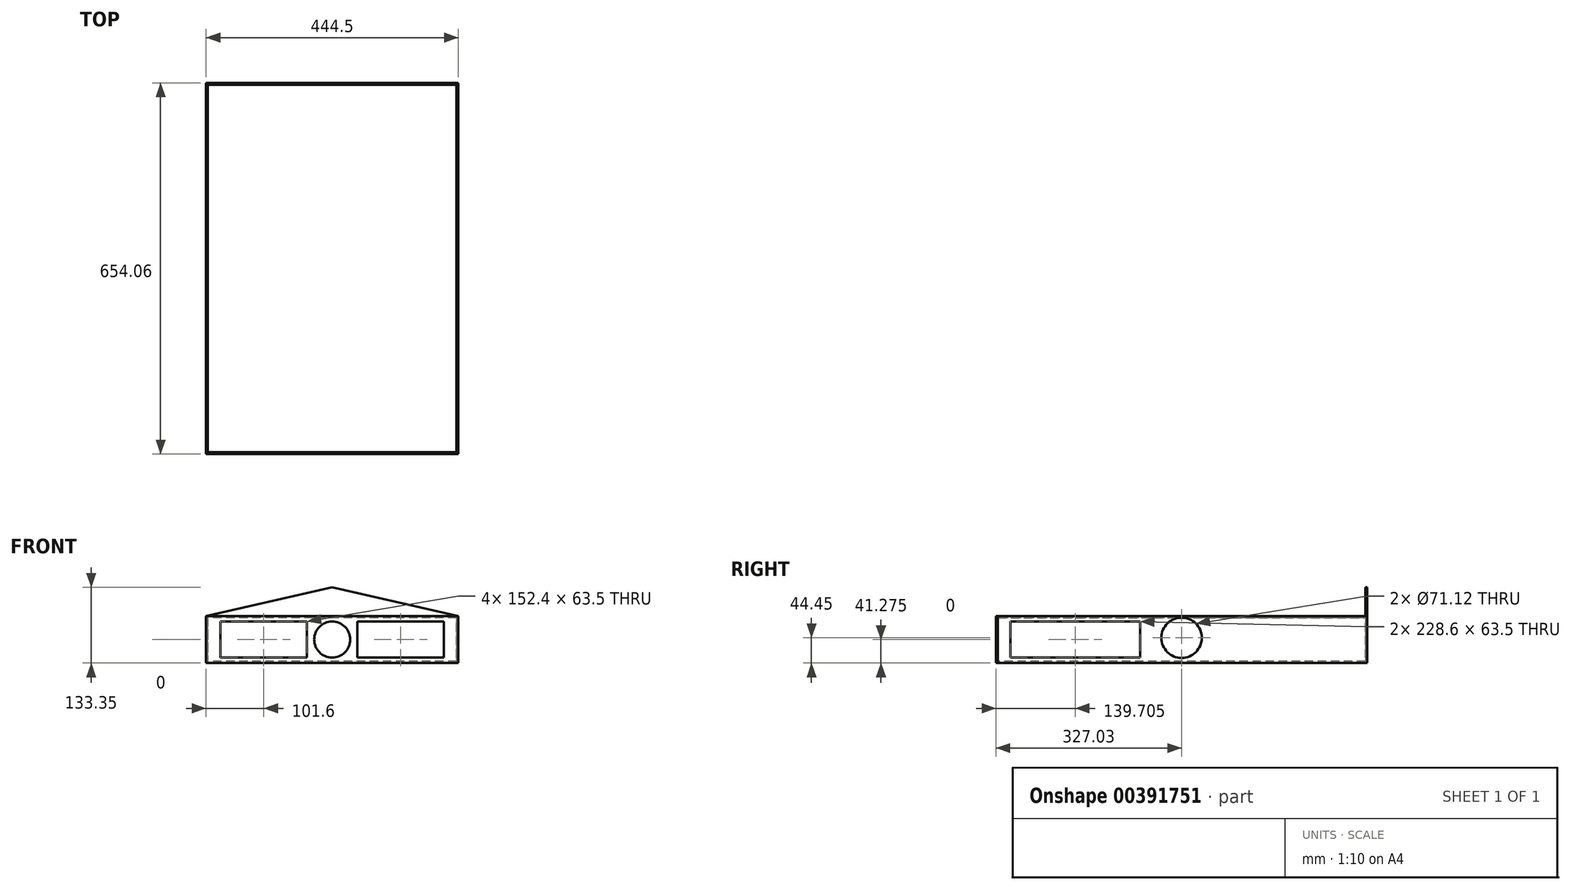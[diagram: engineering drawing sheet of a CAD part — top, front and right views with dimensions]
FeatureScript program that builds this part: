
annotation { "Feature Type Name" : "Feature", "Feature Type Description" : "" }
export const myFeature = defineFeature(function(context is Context, id is Id, definition is map)
    precondition{}
    {
        {
            var Q0;
            Q0=qCreatedBy(makeId("Top.planeOp"),FACE);
            var sketch = newSketch(context, id + "F0", { "sketchPlane" : qUnion([Q0])});
            skLineSegment(sketch, "E0.bottom", {"start": v(219.08, 323.85) * mm, "end": v(-219.07, 323.85) * mm});
            skLineSegment(sketch, "E0.top", {"start": v(219.07, -323.85) * mm, "end": v(-219.08, -323.85) * mm});
            skLineSegment(sketch, "E0.left", {"start": v(219.08, 323.85) * mm, "end": v(219.07, -323.85) * mm});
            skLineSegment(sketch, "E0.right", {"start": v(-219.07, 323.85) * mm, "end": v(-219.08, -323.85) * mm});
            skPoint(sketch, "E0.middle", {"position": v(0, 0) * mm});
            skSolve(sketch);
        }
        {
            var Q0;
            Q0=qSketchRegion(id+"F0",true);
            extrude(context, id + "F1", {"entities" : qUnion([Q0]), "depth" : 3.17 * mm});
        }
        {
            var Q0;
            Q0=makeQuery(id+"F1.opExtrude","CAP_FACE",FACE,{"disambiguationData":[OSD([sQuery(id+"F0.wireOp",EDGE,"E0.bottom"),sQuery(id+"F0.wireOp",EDGE,"E0.top"),sQuery(id+"F0.wireOp",EDGE,"E0.left"),sQuery(id+"F0.wireOp",EDGE,"E0.right")])],"isStart":true});
            var sketch = newSketch(context, id + "F2", { "sketchPlane" : qUnion([Q0])});
            skLineSegment(sketch, "E1.bottom", {"start": v(222.25, 327.03) * mm, "end": v(-222.25, 327.03) * mm});
            skLineSegment(sketch, "E1.top", {"start": v(222.25, -327.03) * mm, "end": v(-222.25, -327.03) * mm});
            skLineSegment(sketch, "E1.left", {"start": v(222.25, 327.03) * mm, "end": v(222.25, -327.03) * mm});
            skLineSegment(sketch, "E1.right", {"start": v(-222.25, 327.03) * mm, "end": v(-222.25, -327.03) * mm});
            skPoint(sketch, "E1.middle", {"position": v(0, 0) * mm});
            skLineSegment(sketch, "E2.bottom", {"start": v(219.07, 323.85) * mm, "end": v(-219.07, 323.85) * mm});
            skLineSegment(sketch, "E2.top", {"start": v(219.07, -323.85) * mm, "end": v(-219.07, -323.85) * mm});
            skLineSegment(sketch, "E2.left", {"start": v(219.07, 323.85) * mm, "end": v(219.07, -323.85) * mm});
            skLineSegment(sketch, "E2.right", {"start": v(-219.07, 323.85) * mm, "end": v(-219.07, -323.85) * mm});
            skLineSegment(sketch, "E3", {"start": v(219.07, 323.85) * mm, "end": v(222.25, 323.85) * mm});
            skLineSegment(sketch, "E4", {"start": v(-219.07, 323.85) * mm, "end": v(-222.25, 323.85) * mm});
            skLineSegment(sketch, "E5", {"start": v(-219.07, -323.85) * mm, "end": v(-222.25, -323.85) * mm});
            skLineSegment(sketch, "E6", {"start": v(219.07, -323.85) * mm, "end": v(222.25, -321.74) * mm});
            skSolve(sketch);
        }
        {
            var Q0;
            {var subQ1=sQuery(id+"F2.wireOp",EDGE,"E1.bottom");Q0=makeQuery(id+"F2.imprint","IMPRINT",FACE,{"disambiguationData":[TD([[makeQuery(id+"F2.imprint","IMPRINT",EDGE,{"derivedFrom":subQ1}),1.0]])]});}
            var Q1;
            {var subQ1=sQuery(id+"F2.wireOp",EDGE,"E1.top");Q1=makeQuery(id+"F2.imprint","IMPRINT",FACE,{"disambiguationData":[TD([[makeQuery(id+"F2.imprint","IMPRINT",EDGE,{"derivedFrom":subQ1}),-1.0]])]});}
            var Q2;
            Q2=makeQuery(id+"F1.opExtrude","CAP_FACE",FACE,{"disambiguationData":[OSD([sQuery(id+"F0.wireOp",EDGE,"E0.bottom"),sQuery(id+"F0.wireOp",EDGE,"E0.top"),sQuery(id+"F0.wireOp",EDGE,"E0.left"),sQuery(id+"F0.wireOp",EDGE,"E0.right")])],"isStart":false});
            extrude(context, id + "F3", {"entities" : qUnion([Q0, Q1]), "oppositeDirection" : true, "depth" : 82.55 * mm});
        }
        {
            var Q0;
            Q0=makeQuery(id+"F2.imprint","IMPRINT",FACE,{"disambiguationData":[TD([[makeQuery(id+"F2.imprint","IMPRINT",EDGE,{"derivedFrom":sQuery(id+"F2.wireOp",EDGE,"E2.left")}),-1.0]])]});
            var Q1;
            Q1=makeQuery(id+"F2.imprint","IMPRINT",FACE,{"disambiguationData":[TD([[makeQuery(id+"F2.imprint","IMPRINT",EDGE,{"derivedFrom":sQuery(id+"F2.wireOp",EDGE,"E2.right")}),1.0]])]});
            var Q2;
            Q2=makeQuery(id+"F3.opExtrude","CAP_FACE",FACE,{"disambiguationData":[OSD([sQuery(id+"F2.wireOp",EDGE,"E1.top"),sQuery(id+"F2.wireOp",EDGE,"E1.left"),sQuery(id+"F2.wireOp",EDGE,"E1.right"),sQuery(id+"F2.wireOp",EDGE,"E2.top"),sQuery(id+"F2.wireOp",EDGE,"E5"),sQuery(id+"F2.wireOp",EDGE,"E6")])],"isStart":false});
            extrude(context, id + "F4", {"entities" : qUnion([Q0, Q1]), "endBound" : BoundingType.UP_TO_SURFACE, "oppositeDirection" : true, "endBoundEntityFace" : qUnion([Q2]), "depth" : 25.4 * mm});
        }
        {
            var Q0;
            Q0=makeQuery(id+"F4.opExtrude","SWEPT_FACE",FACE,{"disambiguationData":[OSD([sQuery(id+"F2.wireOp",EDGE,"E1.right")])]});
            var sketch = newSketch(context, id + "F5", { "sketchPlane" : qUnion([Q0])});
            skCircle(sketch, "E7", {"center": v(0, 44.45) * mm, "radius": 35.56 * mm});
            skSolve(sketch);
        }
        {
            var Q0;
            Q0=makeQuery(id+"F5.imprint","IMPRINT",FACE,{"disambiguationData":[TD([[makeQuery(id+"F5.imprint","IMPRINT",EDGE,{"derivedFrom":sQuery(id+"F5.wireOp",EDGE,"E7")}),1.0]])]});
            extrude(context, id + "F6", {"entities" : qUnion([Q0]), "operationType" : NewBodyOperationType.REMOVE, "endBound" : BoundingType.THROUGH_ALL, "oppositeDirection" : true, "depth" : 25.4 * mm});
        }
        {
            var Q0;
            Q0=makeQuery(id+"F4.opExtrude","SWEPT_FACE",FACE,{"disambiguationData":[OSD([sQuery(id+"F2.wireOp",EDGE,"E1.right")])]});
            var sketch = newSketch(context, id + "F7", { "sketchPlane" : qUnion([Q0])});
            skLineSegment(sketch, "E8.bottom", {"start": v(200.03, 73.03) * mm, "end": v(301.63, 73.03) * mm});
            skLineSegment(sketch, "E8.top", {"start": v(200.03, 47.63) * mm, "end": v(301.63, 47.63) * mm});
            skLineSegment(sketch, "E8.left", {"start": v(200.03, 73.03) * mm, "end": v(200.03, 47.63) * mm});
            skLineSegment(sketch, "E8.right", {"start": v(301.63, 73.03) * mm, "end": v(301.63, 47.63) * mm});
            skLineSegment(sketch, "E9.bottom", {"start": v(263.53, 34.92) * mm, "end": v(301.63, 34.92) * mm});
            skLineSegment(sketch, "E9.top", {"start": v(263.53, 9.53) * mm, "end": v(301.63, 9.53) * mm});
            skLineSegment(sketch, "E9.left", {"start": v(263.53, 34.92) * mm, "end": v(263.53, 9.52) * mm});
            skLineSegment(sketch, "E9.right", {"start": v(301.63, 34.92) * mm, "end": v(301.63, 9.52) * mm});
            skLineSegment(sketch, "E10", {"start": v(250.83, 47.63) * mm, "end": v(250.83, 34.92) * mm, "construction": true});
            skLineSegment(sketch, "E11", {"start": v(250.83, 34.92) * mm, "end": v(263.53, 34.92) * mm, "construction": true});
            skLineSegment(sketch, "E12.bottom", {"start": v(238.13, 34.92) * mm, "end": v(136.53, 34.92) * mm});
            skLineSegment(sketch, "E12.top", {"start": v(238.13, 9.53) * mm, "end": v(136.53, 9.52) * mm});
            skLineSegment(sketch, "E12.left", {"start": v(238.13, 34.92) * mm, "end": v(238.13, 9.53) * mm});
            skLineSegment(sketch, "E12.right", {"start": v(136.53, 34.92) * mm, "end": v(136.53, 9.52) * mm});
            skLineSegment(sketch, "E13", {"start": v(238.13, 34.92) * mm, "end": v(250.83, 34.92) * mm, "construction": true});
            skLineSegment(sketch, "E14", {"start": v(263.53, 9.53) * mm, "end": v(263.53, 0) * mm, "construction": true});
            skLineSegment(sketch, "E15", {"start": v(250.83, 73.03) * mm, "end": v(250.83, 82.55) * mm, "construction": true});
            skLineSegment(sketch, "E16.bottom", {"start": v(174.63, 73.03) * mm, "end": v(73.03, 73.03) * mm});
            skLineSegment(sketch, "E16.top", {"start": v(174.63, 47.63) * mm, "end": v(73.03, 47.63) * mm});
            skLineSegment(sketch, "E16.left", {"start": v(174.63, 73.03) * mm, "end": v(174.63, 47.63) * mm});
            skLineSegment(sketch, "E16.right", {"start": v(73.03, 73.03) * mm, "end": v(73.03, 47.63) * mm});
            skLineSegment(sketch, "E17", {"start": v(174.63, 60.33) * mm, "end": v(187.33, 60.33) * mm, "construction": true});
            skLineSegment(sketch, "E18", {"start": v(187.33, 60.33) * mm, "end": v(200.03, 60.33) * mm, "construction": true});
            skLineSegment(sketch, "E19.bottom", {"start": v(73.03, 34.92) * mm, "end": v(111.13, 34.92) * mm});
            skLineSegment(sketch, "E19.top", {"start": v(73.03, 9.52) * mm, "end": v(111.13, 9.52) * mm});
            skLineSegment(sketch, "E19.left", {"start": v(73.03, 34.92) * mm, "end": v(73.03, 9.52) * mm});
            skLineSegment(sketch, "E19.right", {"start": v(111.13, 34.92) * mm, "end": v(111.13, 9.52) * mm});
            skLineSegment(sketch, "E20", {"start": v(174.63, 73.03) * mm, "end": v(200.03, 73.03) * mm});
            skLineSegment(sketch, "E21", {"start": v(111.13, 9.52) * mm, "end": v(136.53, 9.52) * mm});
            skLineSegment(sketch, "E22", {"start": v(73.03, 34.92) * mm, "end": v(73.03, 47.63) * mm});
            skLineSegment(sketch, "E23", {"start": v(301.63, 47.63) * mm, "end": v(301.63, 34.92) * mm});
            skLineSegment(sketch, "E24", {"start": v(238.13, 9.53) * mm, "end": v(263.53, 9.53) * mm});
            skSolve(sketch);
        }
        {
            var Q0;
            Q0=qSketchRegion(id+"F7",true);
            extrude(context, id + "F8", {"entities" : qUnion([Q0]), "operationType" : NewBodyOperationType.REMOVE, "endBound" : BoundingType.THROUGH_ALL, "oppositeDirection" : true, "depth" : 25.4 * mm});
        }
        {
            var Q0;
            Q0=makeQuery(id+"F3.opExtrude","SWEPT_FACE",FACE,{"disambiguationData":[OSD([sQuery(id+"F2.wireOp",EDGE,"E1.bottom")])]});
            var sketch = newSketch(context, id + "F9", { "sketchPlane" : qUnion([Q0])});
            skLineSegment(sketch, "E25.bottom", {"start": v(-196.85, 73.03) * mm, "end": v(196.85, 73.03) * mm});
            skLineSegment(sketch, "E25.top", {"start": v(-196.85, 9.52) * mm, "end": v(196.85, 9.52) * mm});
            skLineSegment(sketch, "E25.left", {"start": v(-196.85, 73.03) * mm, "end": v(-196.85, 9.52) * mm});
            skLineSegment(sketch, "E25.right", {"start": v(196.85, 73.03) * mm, "end": v(196.85, 9.52) * mm});
            skPoint(sketch, "E25.middle", {"position": v(0, 41.28) * mm});
            skLineSegment(sketch, "E26.bottom", {"start": v(6.35, 73.03) * mm, "end": v(-6.35, 73.03) * mm});
            skLineSegment(sketch, "E26.top", {"start": v(6.35, 9.52) * mm, "end": v(-6.35, 9.52) * mm});
            skLineSegment(sketch, "E26.left", {"start": v(6.35, 73.03) * mm, "end": v(6.35, 9.52) * mm});
            skLineSegment(sketch, "E26.right", {"start": v(-6.35, 73.03) * mm, "end": v(-6.35, 9.52) * mm});
            skCircle(sketch, "E27", {"center": v(0, 41.28) * mm, "radius": 31.75 * mm});
            skLineSegment(sketch, "E28.bottom", {"start": v(44.45, 73.03) * mm, "end": v(-44.45, 73.03) * mm});
            skLineSegment(sketch, "E28.top", {"start": v(44.45, 9.52) * mm, "end": v(-44.45, 9.52) * mm});
            skLineSegment(sketch, "E28.left", {"start": v(44.45, 73.03) * mm, "end": v(44.45, 9.52) * mm});
            skLineSegment(sketch, "E28.right", {"start": v(-44.45, 73.03) * mm, "end": v(-44.45, 9.52) * mm});
            skSolve(sketch);
        }
        {
            var Q0;
            {var subQ0=sQuery(id+"F9.wireOp",EDGE,"E25.left");Q0=makeQuery(id+"F9.imprint","IMPRINT",FACE,{"disambiguationData":[TD([[makeQuery(id+"F9.imprint","IMPRINT",EDGE,{"derivedFrom":subQ0}),1.0]])]});}
            var Q1;
            {var subQ0=sQuery(id+"F9.wireOp",EDGE,"E25.right");Q1=makeQuery(id+"F9.imprint","IMPRINT",FACE,{"disambiguationData":[TD([[makeQuery(id+"F9.imprint","IMPRINT",EDGE,{"derivedFrom":subQ0}),-1.0]])]});}
            var Q2;
            {var subQ0=sQuery(id+"F9.wireOp",EDGE,"E27");var subQ1=sQuery(id+"F9.wireOp",EDGE,"E26.right");var subQ2=makeQuery(id+"F9.imprint","INTERSECT",VERTEX,{"disambiguationData":[OD(0.0)],"derivedFrom":[subQ1,subQ0]});Q2=makeQuery(id+"F9.imprint","IMPRINT",FACE,{"disambiguationData":[TD([[makeQuery(id+"F9.imprint","IMPRINT",EDGE,{"disambiguationData":[TD([[subQ2,-1.0]])],"derivedFrom":subQ1}),-1.0]])]});}
            var Q3;
            {var subQ0=sQuery(id+"F9.wireOp",EDGE,"E27");var subQ5=sQuery(id+"F9.wireOp",EDGE,"E26.left");var subQ6=makeQuery(id+"F9.imprint","INTERSECT",VERTEX,{"disambiguationData":[OD(0.0)],"derivedFrom":[subQ5,subQ0]});Q3=makeQuery(id+"F9.imprint","IMPRINT",FACE,{"disambiguationData":[TD([[makeQuery(id+"F9.imprint","IMPRINT",EDGE,{"disambiguationData":[TD([[subQ6,-1.0]])],"derivedFrom":subQ5}),-1.0]])]});}
            var Q4;
            {var subQ0=sQuery(id+"F9.wireOp",EDGE,"E27");var subQ1=sQuery(id+"F9.wireOp",EDGE,"E26.left");var subQ2=makeQuery(id+"F9.imprint","INTERSECT",VERTEX,{"disambiguationData":[OD(0.0)],"derivedFrom":[subQ1,subQ0]});Q4=makeQuery(id+"F9.imprint","IMPRINT",FACE,{"disambiguationData":[TD([[makeQuery(id+"F9.imprint","IMPRINT",EDGE,{"disambiguationData":[TD([[subQ2,-1.0]])],"derivedFrom":subQ1}),1.0]])]});}
            extrude(context, id + "F10", {"entities" : qUnion([Q0, Q1, Q2, Q3, Q4]), "operationType" : NewBodyOperationType.REMOVE, "endBound" : BoundingType.THROUGH_ALL, "oppositeDirection" : true, "depth" : 25.4 * mm});
        }
        {
            var Q0;
            Q0=makeQuery(id+"F4.opExtrude","CAP_FACE",FACE,{"disambiguationData":[OSD([sQuery(id+"F2.wireOp",EDGE,"E1.left"),sQuery(id+"F2.wireOp",EDGE,"E2.left"),sQuery(id+"F2.wireOp",EDGE,"E3"),sQuery(id+"F2.wireOp",EDGE,"E6")])],"isStart":true});
            var sketch = newSketch(context, id + "F11", { "sketchPlane" : qUnion([Q0])});
            skLineSegment(sketch, "E29.bottom", {"start": v(219.07, 323.85) * mm, "end": v(-219.08, 323.85) * mm});
            skLineSegment(sketch, "E29.top", {"start": v(219.08, -323.85) * mm, "end": v(-219.07, -323.85) * mm});
            skLineSegment(sketch, "E29.left", {"start": v(219.07, 323.85) * mm, "end": v(219.08, -323.85) * mm});
            skLineSegment(sketch, "E29.right", {"start": v(-219.08, 323.85) * mm, "end": v(-219.07, -323.85) * mm});
            skSolve(sketch);
        }
        {
            var Q0;
            Q0=qSketchRegion(id+"F11",true);
            extrude(context, id + "F12", {"entities" : qUnion([Q0]), "oppositeDirection" : true, "depth" : 79.38 * mm});
        }
        {
            var Q0;
            Q0=makeQuery(id+"F3.opExtrude","SWEPT_FACE",FACE,{"disambiguationData":[OSD([sQuery(id+"F2.wireOp",EDGE,"E1.top")])]});
            var sketch = newSketch(context, id + "F13", { "sketchPlane" : qUnion([Q0])});
            skLineSegment(sketch, "E30", {"start": v(-222.25, 82.55) * mm, "end": v(0, 133.35) * mm});
            skLineSegment(sketch, "E31", {"start": v(0, 133.35) * mm, "end": v(222.25, 82.55) * mm});
            skLineSegment(sketch, "E32", {"start": v(222.25, 82.55) * mm, "end": v(-222.25, 82.55) * mm});
            skLineSegment(sketch, "E33", {"start": v(0, 133.35) * mm, "end": v(0, 82.55) * mm});
            skSolve(sketch);
        }
        {
            var Q0;
            {var subQ0=sQuery(id+"F13.wireOp",EDGE,"E31");Q0=makeQuery(id+"F13.imprint","IMPRINT",FACE,{"disambiguationData":[TD([[makeQuery(id+"F13.imprint","IMPRINT",EDGE,{"derivedFrom":subQ0}),-1.0]])]});}
            var Q1;
            {var subQ0=sQuery(id+"F13.wireOp",EDGE,"E30");Q1=makeQuery(id+"F13.imprint","IMPRINT",FACE,{"disambiguationData":[TD([[makeQuery(id+"F13.imprint","IMPRINT",EDGE,{"derivedFrom":subQ0}),-1.0]])]});}
            var Q2;
            Q2=makeQuery(id+"F3.opExtrude","SWEPT_FACE",FACE,{"disambiguationData":[OSD([sQuery(id+"F2.wireOp",EDGE,"E2.top"),sQuery(id+"F2.wireOp",EDGE,"E5")])]});
            extrude(context, id + "F14", {"entities" : qUnion([Q0, Q1]), "operationType" : NewBodyOperationType.ADD, "endBound" : BoundingType.UP_TO_SURFACE, "oppositeDirection" : true, "endBoundEntityFace" : qUnion([Q2]), "depth" : 3.17 * mm});
        }
    });
